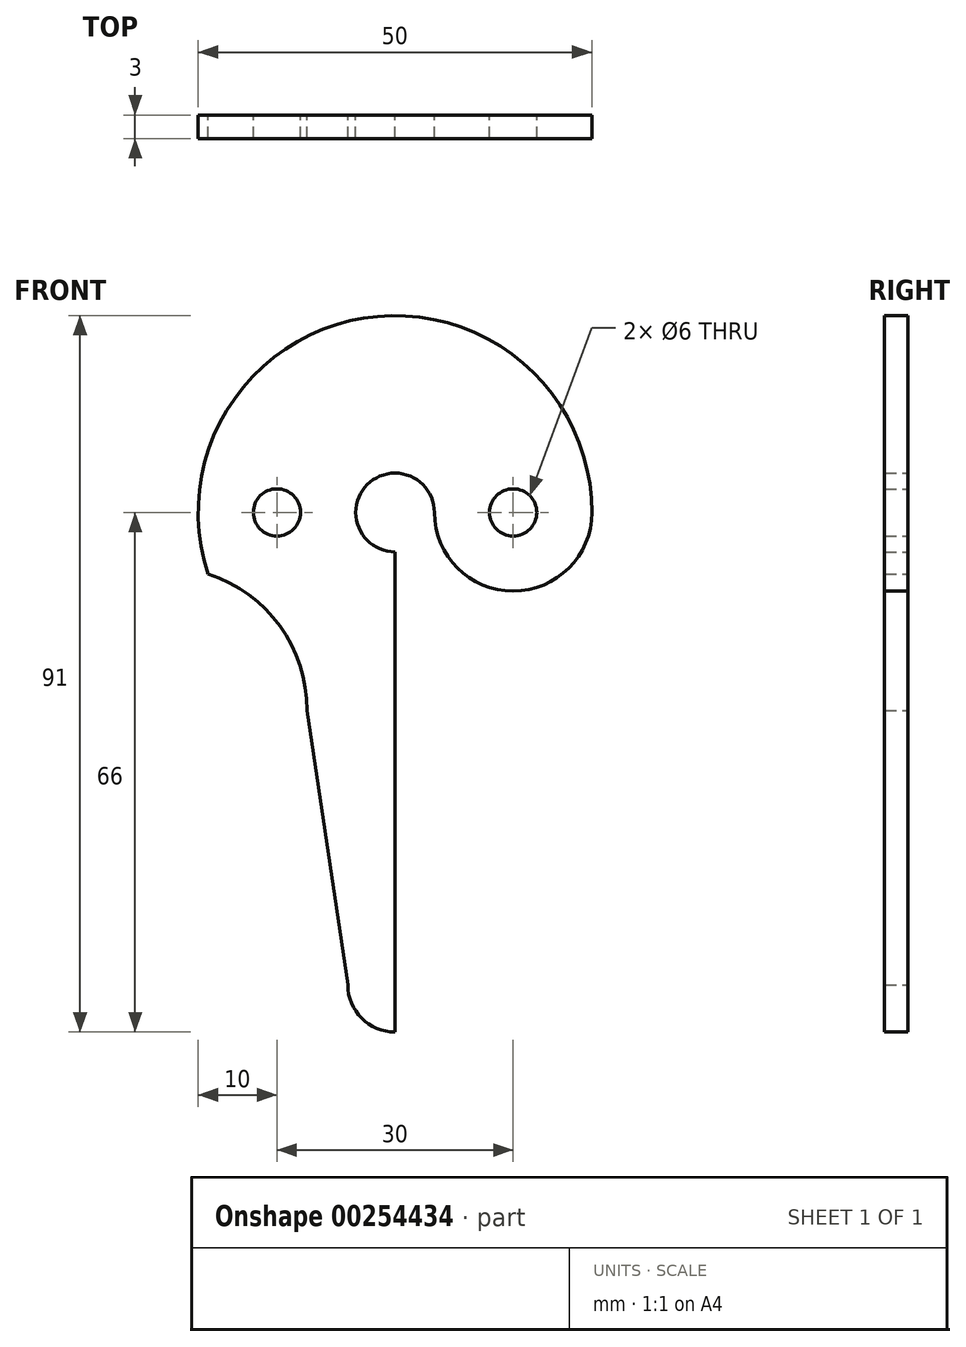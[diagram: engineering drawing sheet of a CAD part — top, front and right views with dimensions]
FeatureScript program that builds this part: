
annotation { "Feature Type Name" : "Feature", "Feature Type Description" : "" }
export const myFeature = defineFeature(function(context is Context, id is Id, definition is map)
    precondition{}
    {
        {
            var Q0;
            Q0=qCreatedBy(makeId("Front.planeOp"),FACE);
            var sketch = newSketch(context, id + "F0", { "sketchPlane" : qUnion([Q0])});
            skArc(sketch, "E0", {"start": v(25, 0) * mm, "mid": v(-3.97, 24.68) * mm, "end": v(-23.74, -7.85) * mm});
            skPoint(sketch, "E1", {"position": v(15, 0) * mm});
            skPoint(sketch, "E2", {"position": v(-15, 0) * mm});
            skArc(sketch, "E3", {"start": v(5, 0) * mm, "mid": v(-3.54, 3.54) * mm, "end": v(0, -5) * mm});
            skCircle(sketch, "E4", {"center": v(-15, 0) * mm, "radius": 3 * mm});
            skCircle(sketch, "E5", {"center": v(15, 0) * mm, "radius": 3 * mm});
            skPoint(sketch, "E6", {"position": v(-29.19, -25) * mm});
            skArc(sketch, "E7", {"start": v(-11.19, -25.13) * mm, "mid": v(-14.62, -14.43) * mm, "end": v(-23.74, -7.85) * mm});
            skPoint(sketch, "E8", {"position": v(0, -60) * mm});
            skArc(sketch, "E9", {"start": v(-6, -60) * mm, "mid": v(-4.24, -64.24) * mm, "end": v(0, -66) * mm});
            skLineSegment(sketch, "E10", {"start": v(-12, -19.63) * mm, "end": v(-6, -60) * mm});
            skLineSegment(sketch, "E11", {"start": v(0, 0) * mm, "end": v(0, -60) * mm});
            skArc(sketch, "E12", {"start": v(5, 0) * mm, "mid": v(15, -10) * mm, "end": v(25, 0) * mm});
            skArc(sketch, "E13.trimOffspring", {"start": v(-11.64, -22.13) * mm, "mid": v(-11.52, -22.19) * mm, "end": v(-11.4, -22.25) * mm});
            skLineSegment(sketch, "E14", {"start": v(0, -60) * mm, "end": v(0, -66) * mm});
            skSolve(sketch);
        }
        {
            var Q0;
            {var subQ4=sQuery(id+"F0.wireOp",EDGE,"E0");Q0=makeQuery(id+"F0.imprint","IMPRINT",FACE,{"disambiguationData":[TD([[makeQuery(id+"F0.imprint","IMPRINT",EDGE,{"derivedFrom":subQ4}),1.0]])]});}
            extrude(context, id + "F1", {"entities" : qUnion([Q0]), "depth" : 3 * mm});
        }
    });
